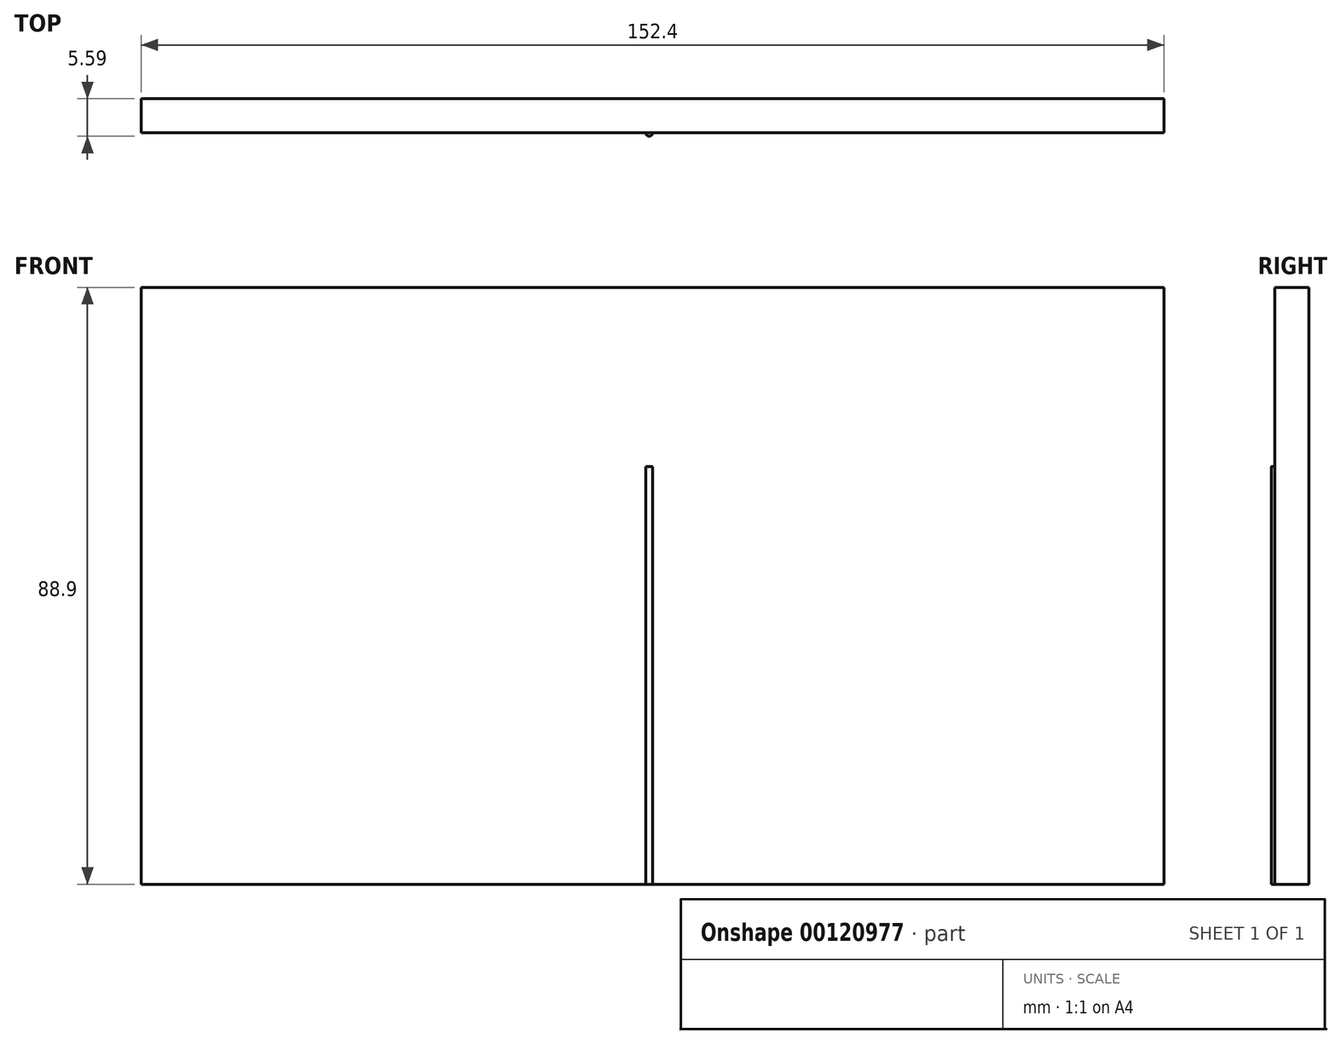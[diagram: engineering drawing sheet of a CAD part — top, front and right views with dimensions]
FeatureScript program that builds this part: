
annotation { "Feature Type Name" : "Feature", "Feature Type Description" : "" }
export const myFeature = defineFeature(function(context is Context, id is Id, definition is map)
    precondition{}
    {
        {
            var Q0;
            Q0=qCreatedBy(makeId("Front.planeOp"),FACE);
            var sketch = newSketch(context, id + "F0", { "sketchPlane" : qUnion([Q0])});
            skLineSegment(sketch, "E0.bottom", {"start": v(-110.02, 20.94) * mm, "end": v(42.38, 20.94) * mm});
            skLineSegment(sketch, "E0.top", {"start": v(-110.02, -67.96) * mm, "end": v(42.38, -67.96) * mm});
            skLineSegment(sketch, "E0.right", {"start": v(42.38, 20.94) * mm, "end": v(42.38, -67.96) * mm});
            skLineSegment(sketch, "E1", {"start": v(-110.02, 20.94) * mm, "end": v(-110.02, -67.96) * mm});
            skPoint(sketch, "E2", {"position": v(-33.82, -67.96) * mm});
            skLineSegment(sketch, "E3", {"start": v(-33.82, -5.73) * mm, "end": v(-33.82, -67.96) * mm});
            skLineSegment(sketch, "E4.0", {"start": v(-34.33, -5.73) * mm, "end": v(-34.33, -67.96) * mm});
            skLineSegment(sketch, "E5", {"start": v(-34.33, -5.73) * mm, "end": v(-33.82, -5.73) * mm});
            skSolve(sketch);
        }
        {
            var Q0;
            Q0=qSketchRegion(id+"F0",true);
            extrude(context, id + "F1", {"entities" : qUnion([Q0]), "oppositeDirection" : true, "depth" : 5.08 * mm});
        }
        {
            var Q0;
            {var subQ0=sQuery(id+"F0.wireOp",EDGE,"E3");Q0=makeQuery(id+"F0.imprint","IMPRINT",FACE,{"disambiguationData":[TD([[makeQuery(id+"F0.imprint","IMPRINT",EDGE,{"derivedFrom":subQ0}),-1.0]])]});}
            var Q1;
            Q1=sQuery(id+"F0.wireOp",EDGE,"E4.0");
            revolve(context, id + "F2", {"operationType" : NewBodyOperationType.ADD, "entities" : qUnion([Q0]), "axis" : qUnion([Q1]), "revolveType" : RevolveType.FULL});
        }
    });
